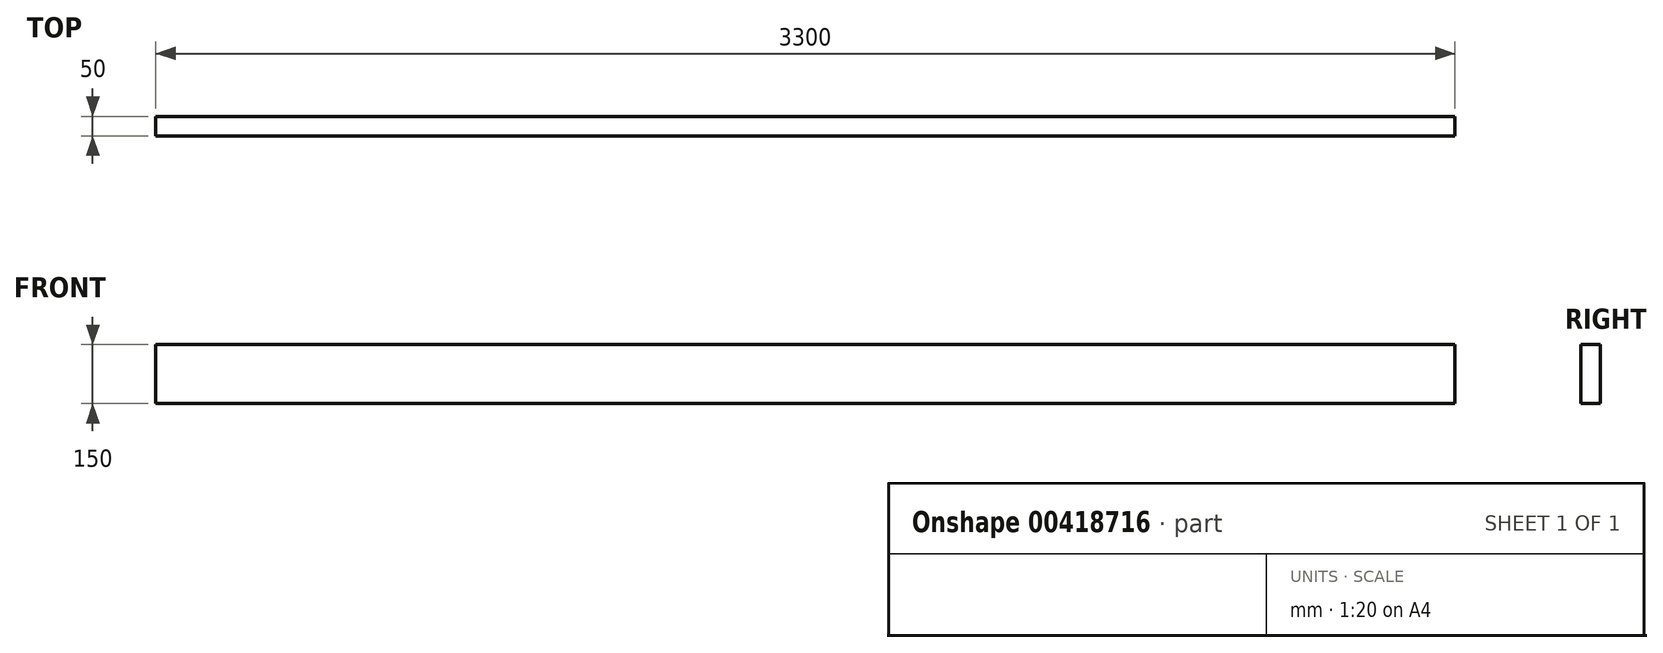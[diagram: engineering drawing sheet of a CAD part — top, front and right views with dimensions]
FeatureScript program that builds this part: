
annotation { "Feature Type Name" : "Feature", "Feature Type Description" : "" }
export const myFeature = defineFeature(function(context is Context, id is Id, definition is map)
    precondition{}
    {
        {
            var Q0;
            Q0=qCreatedBy(makeId("Right.planeOp"),FACE);
            var sketch = newSketch(context, id + "F0", { "sketchPlane" : qUnion([Q0])});
            skLineSegment(sketch, "E0.bottom", {"start": v(25, 75) * mm, "end": v(-25, 75) * mm});
            skLineSegment(sketch, "E0.top", {"start": v(25, -75) * mm, "end": v(-25, -75) * mm});
            skLineSegment(sketch, "E0.left", {"start": v(25, 75) * mm, "end": v(25, -75) * mm});
            skLineSegment(sketch, "E0.right", {"start": v(-25, 75) * mm, "end": v(-25, -75) * mm});
            skPoint(sketch, "E0.middle", {"position": v(0, 0) * mm});
            skSolve(sketch);
        }
        {
            var Q0;
            Q0 = qSketchRegion(id + "F0", true);
            extrude(context, id + "F1", {"entities" : qUnion([Q0]), "endBound" : BoundingType.SYMMETRIC, "oppositeDirection" : true, "depth" : 3300 * mm});
        }
    });
